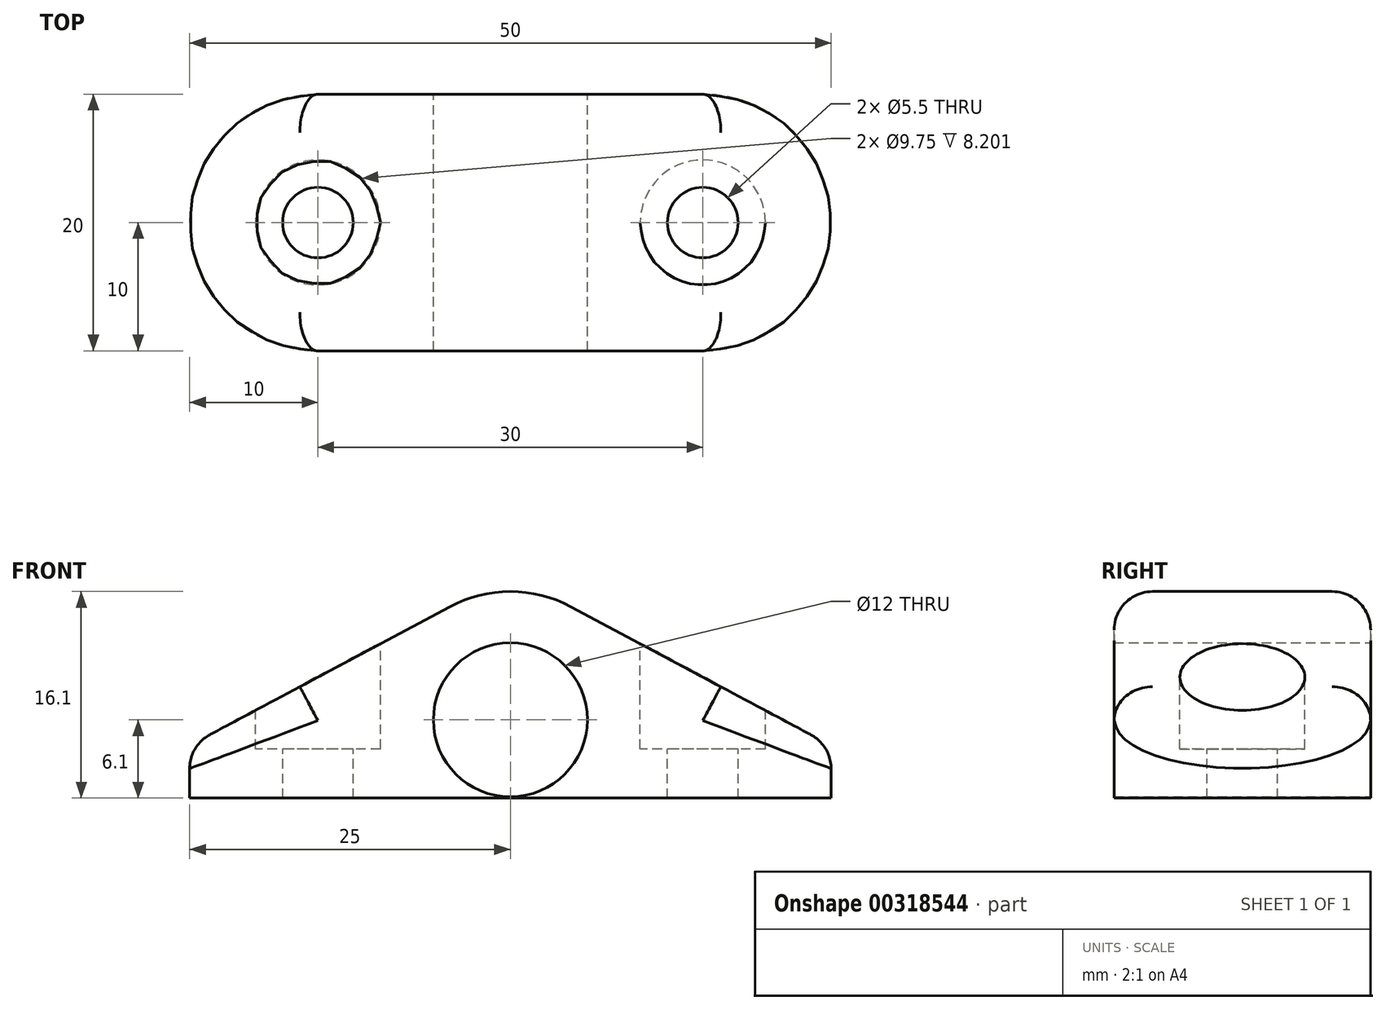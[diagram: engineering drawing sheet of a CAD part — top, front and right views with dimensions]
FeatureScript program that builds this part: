
annotation { "Feature Type Name" : "Feature", "Feature Type Description" : "" }
export const myFeature = defineFeature(function(context is Context, id is Id, definition is map)
    precondition{}
    {
        {
            var Q0;
            Q0=qCreatedBy(makeId("Front.planeOp"),FACE);
            var sketch = newSketch(context, id + "F0", { "sketchPlane" : qUnion([Q0])});
            skCircle(sketch, "E0", {"center": v(0, 10) * mm, "radius": 10 * mm});
            skLineSegment(sketch, "E1", {"start": v(-25, 0) * mm, "end": v(25, 0) * mm});
            skLineSegment(sketch, "E2", {"start": v(25, 0) * mm, "end": v(25, 8) * mm});
            skLineSegment(sketch, "E3", {"start": v(25, 8) * mm, "end": v(-25, 8) * mm});
            skLineSegment(sketch, "E4", {"start": v(-25, 8) * mm, "end": v(-25, 0) * mm});
            skCircle(sketch, "E5", {"center": v(0, 10) * mm, "radius": 6 * mm});
            skLineSegment(sketch, "E6", {"start": v(-25, 8) * mm, "end": v(3.28, 8) * mm});
            skLineSegment(sketch, "E7", {"start": v(0, 41.76) * mm, "end": v(0, -22.03) * mm, "construction": true});
            skLineSegment(sketch, "E8", {"start": v(3.28, 8) * mm, "end": v(-4.72, 18.82) * mm});
            skLineSegment(sketch, "E9", {"start": v(-4.72, 18.82) * mm, "end": v(-25, 8) * mm});
            skLineSegment(sketch, "E10.MirrorCS", {"start": v(25, 8) * mm, "end": v(-3.28, 8) * mm});
            skLineSegment(sketch, "E11.MirrorCS", {"start": v(4.72, 18.82) * mm, "end": v(25, 8) * mm});
            skLineSegment(sketch, "E12.MirrorCS", {"start": v(-3.28, 8) * mm, "end": v(4.72, 18.82) * mm});
            skSolve(sketch);
        }
        {
            var Q0;
            Q0 = qSketchRegion(id + "F0", true);
            extrude(context, id + "F1", {"entities" : qUnion([Q0]), "depth" : 20 * mm});
        }
        {
            var Q0;
            Q0=makeQuery(id+"F1.opExtrude","CAP_EDGE",EDGE,{"disambiguationData":[OSD([sQuery(id+"F0.wireOp",EDGE,"E4")])],"isStart":false});
            var Q1;
            Q1=makeQuery(id+"F1.opExtrude","CAP_EDGE",EDGE,{"disambiguationData":[OSD([sQuery(id+"F0.wireOp",EDGE,"E4")])],"isStart":true});
            var Q2;
            Q2=makeQuery(id+"F1.opExtrude","CAP_EDGE",EDGE,{"disambiguationData":[OSD([sQuery(id+"F0.wireOp",EDGE,"E2")])],"isStart":false});
            var Q3;
            Q3=makeQuery(id+"F1.opExtrude","CAP_EDGE",EDGE,{"disambiguationData":[OSD([sQuery(id+"F0.wireOp",EDGE,"E2")])],"isStart":true});
            fillet(context, id + "F2", {"entities" : qUnion([Q0, Q1, Q2, Q3]), "radius" : 10 * mm, "tangentPropagation" : true, "allowEdgeOverflow" : false});
        }
        {
            var Q0;
            Q0=makeQuery(id+"F1.opExtrude","SWEPT_FACE",FACE,{"disambiguationData":[OSD([sQuery(id+"F0.wireOp",EDGE,"E1")])]});
            cPlane(context, id + "F3", {"entities" : qUnion([Q0]), "cplaneType" : CPlaneType.OFFSET, "offset" : 25 * mm, "oppositeDirection" : true, "width" : 150 * mm, "height" : 150 * mm});
        }
        {
            var Q0;
            Q0=makeQuery(id+"F1.opExtrude","CAP_EDGE",EDGE,{"disambiguationData":[OSD([sQuery(id+"F0.wireOp",EDGE,"E9")])],"isStart":false});
            var Q1;
            Q1=makeQuery(id+"F1.opExtrude","CAP_EDGE",EDGE,{"disambiguationData":[OSD([sQuery(id+"F0.wireOp",EDGE,"E11.MirrorCS")])],"isStart":false});
            var Q2;
            Q2=makeQuery(id+"F1.opExtrude","CAP_EDGE",EDGE,{"disambiguationData":[OSD([sQuery(id+"F0.wireOp",EDGE,"E0")])],"isStart":false});
            var Q3;
            Q3=makeQuery(id+"F1.opExtrude","CAP_EDGE",EDGE,{"disambiguationData":[OSD([sQuery(id+"F0.wireOp",EDGE,"E0")])],"isStart":true});
            fillet(context, id + "F4", {"entities" : qUnion([Q0, Q1, Q2, Q3]), "radius" : 3 * mm, "tangentPropagation" : true, "allowEdgeOverflow" : false});
        }
        {
            var Q0;
            Q0=qCreatedBy(id+"F3.planeOp",FACE);
            var sketch = newSketch(context, id + "F5", { "sketchPlane" : qUnion([Q0])});
            skPoint(sketch, "E13", {"position": v(-15, 10) * mm});
            skPoint(sketch, "E14", {"position": v(15, 10) * mm});
            skSolve(sketch);
        }
        {
            var Q0;
            Q0=sQuery(id+"F5.wireOp",VERTEX,"E14");
            var Q1;
            Q1=sQuery(id+"F5.wireOp",VERTEX,"E13");
            var Q2;
            Q2=makeQuery(id+"F1.opExtrude","SWEPT_BODY",BODY,{"disambiguationData":[OSD([sQuery(id+"F0.wireOp",EDGE,"E0"),sQuery(id+"F0.wireOp",EDGE,"E1"),sQuery(id+"F0.wireOp",EDGE,"E2"),sQuery(id+"F0.wireOp",EDGE,"E4"),sQuery(id+"F0.wireOp",EDGE,"E5"),sQuery(id+"F0.wireOp",EDGE,"E9"),sQuery(id+"F0.wireOp",EDGE,"E11.MirrorCS")])]});
            hole(context, id + "F6", {"style" : HoleStyle.C_BORE, "endStyle" : HoleEndStyle.THROUGH, "oppositeDirection" : true, "holeDiameter" : 5.5 * mm, "cBoreDiameter" : 9.75 * mm, "cBoreDepth" : 3 * mm, "tappedDepth" : 12 * mm, "tapClearance" : 3, "locations" : qUnion([Q0, Q1]), "scope" : qUnion([Q2])});
        }
        {
            var Q0;
            Q0=makeQuery(id+"F1.opExtrude","CAP_FACE",FACE,{"disambiguationData":[OSD([sQuery(id+"F0.wireOp",EDGE,"E0"),sQuery(id+"F0.wireOp",EDGE,"E1"),sQuery(id+"F0.wireOp",EDGE,"E2"),sQuery(id+"F0.wireOp",EDGE,"E4"),sQuery(id+"F0.wireOp",EDGE,"E5"),sQuery(id+"F0.wireOp",EDGE,"E9"),sQuery(id+"F0.wireOp",EDGE,"E11.MirrorCS")])],"isStart":true});
            var sketch = newSketch(context, id + "F7", { "sketchPlane" : qUnion([Q0])});
            skLineSegment(sketch, "E15.bottom", {"start": v(-26.07, 3.9) * mm, "end": v(27, 3.9) * mm});
            skLineSegment(sketch, "E15.top", {"start": v(-26.07, -4.1) * mm, "end": v(27, -4.1) * mm});
            skLineSegment(sketch, "E15.left", {"start": v(-26.07, 3.9) * mm, "end": v(-26.07, -4.1) * mm});
            skLineSegment(sketch, "E15.right", {"start": v(27, 3.9) * mm, "end": v(27, -4.1) * mm});
            skSolve(sketch);
        }
        {
            var Q0;
            Q0 = qSketchRegion(id + "F7", true);
            extrude(context, id + "F8", {"entities" : qUnion([Q0]), "operationType" : NewBodyOperationType.REMOVE, "oppositeDirection" : true, "depth" : 25 * mm});
        }
    });
